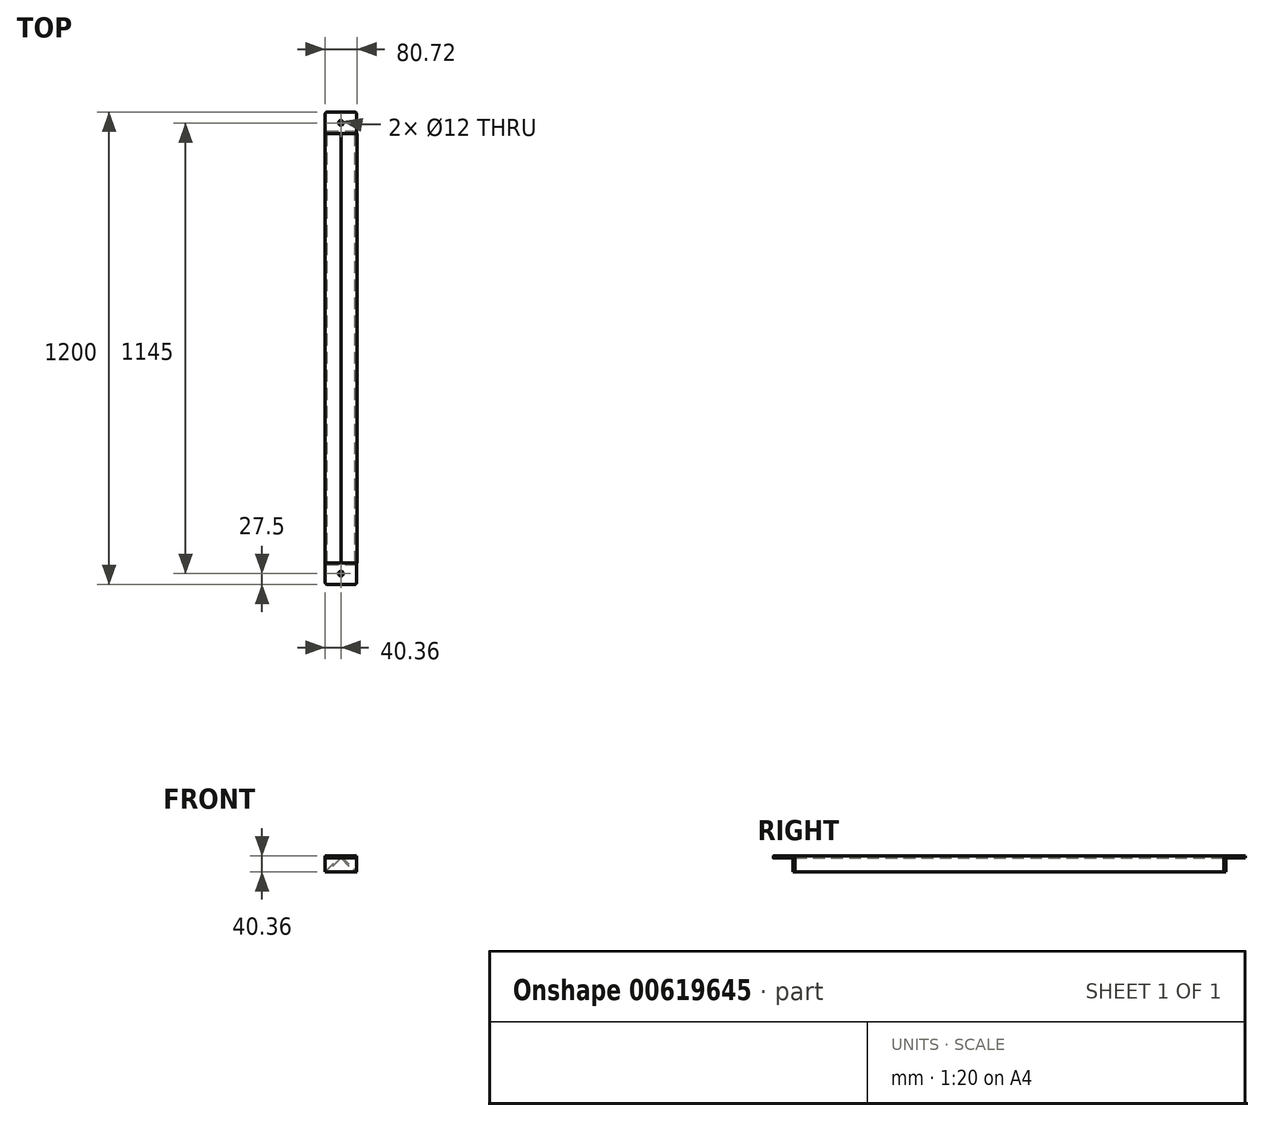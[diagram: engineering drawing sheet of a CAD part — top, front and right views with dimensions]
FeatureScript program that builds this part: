
annotation { "Feature Type Name" : "Feature", "Feature Type Description" : "" }
export const myFeature = defineFeature(function(context is Context, id is Id, definition is map)
    precondition{}
    {
        {
            var Q0;
            Q0=qCreatedBy(makeId("Front.planeOp"),FACE);
            var sketch = newSketch(context, id + "F0", { "sketchPlane" : qUnion([Q0])});
            skLineSegment(sketch, "E0", {"start": v(0, 0) * mm, "end": v(-35.36, -35.36) * mm});
            skLineSegment(sketch, "E1", {"start": v(0, 0) * mm, "end": v(35.36, -35.36) * mm});
            skLineSegment(sketch, "E2", {"start": v(-35.36, -35.36) * mm, "end": v(-40.36, -35.36) * mm});
            skLineSegment(sketch, "E3", {"start": v(-40.36, -35.36) * mm, "end": v(0, 5) * mm});
            skLineSegment(sketch, "E4", {"start": v(35.36, -35.36) * mm, "end": v(40.36, -35.36) * mm});
            skLineSegment(sketch, "E5", {"start": v(0, 5) * mm, "end": v(40.36, -35.36) * mm});
            skSolve(sketch);
        }
        {
            var Q0;
            Q0 = qSketchRegion(id + "F0", true);
            extrude(context, id + "F1", {"entities" : qUnion([Q0]), "depth" : 1090 * mm, "offsetDistance" : 25 * mm});
        }
        {
            var Q0;
            Q0=qCreatedBy(makeId("Right.planeOp"),FACE);
            var sketch = newSketch(context, id + "F2", { "sketchPlane" : qUnion([Q0])});
            skLineSegment(sketch, "E6.0", {"start": v(0, 5) * mm, "end": v(0, -35.36) * mm});
            skLineSegment(sketch, "E7", {"start": v(0, 5) * mm, "end": v(55, 5) * mm});
            skLineSegment(sketch, "E8", {"start": v(55, 5) * mm, "end": v(55, 0) * mm});
            skLineSegment(sketch, "E9", {"start": v(55, 0) * mm, "end": v(5, 0) * mm});
            skLineSegment(sketch, "E10", {"start": v(5, 0) * mm, "end": v(5, -35.36) * mm});
            skLineSegment(sketch, "E11", {"start": v(0, -35.36) * mm, "end": v(5, -35.36) * mm});
            skSolve(sketch);
        }
        {
            var Q0;
            Q0 = qSketchRegion(id + "F2", true);
            extrude(context, id + "F3", {"entities" : qUnion([Q0]), "endBound" : BoundingType.SYMMETRIC, "depth" : 80 * mm, "offsetDistance" : 25 * mm});
        }
        {
            var Q0;
            Q0=makeQuery(id+"F3.opExtrude","SWEPT_FACE",FACE,{"disambiguationData":[OSD([sQuery(id+"F2.wireOp",EDGE,"E7")])]});
            var sketch = newSketch(context, id + "F4", { "sketchPlane" : qUnion([Q0])});
            skPoint(sketch, "E12", {"position": v(0, 27.5) * mm});
            skPoint(sketch, "E12.positionSnap0", {"position": v(0, 55) * mm});
            skPoint(sketch, "E12.positionSnap1", {"position": v(-40, 27.5) * mm});
            skCircle(sketch, "E13", {"center": v(0, 27.5) * mm, "radius": 6 * mm});
            skSolve(sketch);
        }
        {
            var Q0;
            Q0 = qSketchRegion(id + "F4", true);
            extrude(context, id + "F5", {"entities" : qUnion([Q0]), "operationType" : NewBodyOperationType.REMOVE, "oppositeDirection" : true, "depth" : 25 * mm, "offsetDistance" : 25 * mm});
        }
        {
            var Q0;
            Q0=qCreatedBy(makeId("Front.planeOp"),FACE);
            cPlane(context, id + "F6", {"entities" : qUnion([Q0]), "cplaneType" : CPlaneType.OFFSET, "offset" : 545 * mm, "width" : 150 * mm, "height" : 150 * mm});
        }
        {
            var Q0;
            Q0=makeQuery(id+"F3.opExtrude","SWEPT_BODY",BODY,{"disambiguationData":[OSD([sQuery(id+"F2.wireOp",EDGE,"E6.0"),sQuery(id+"F2.wireOp",EDGE,"E7"),sQuery(id+"F2.wireOp",EDGE,"E8"),sQuery(id+"F2.wireOp",EDGE,"E9"),sQuery(id+"F2.wireOp",EDGE,"E10"),sQuery(id+"F2.wireOp",EDGE,"E11")])]});
            var Q1;
            Q1=qCreatedBy(id+"F6.planeOp",FACE);
            mirror(context, id + "F7", {"entities" : qUnion([Q0]), "mirrorPlane" : qUnion([Q1])});
        }
        {
            var Q0;
            Q0=makeQuery(id+"F3.opExtrude","CAP_EDGE",EDGE,{"disambiguationData":[OSD([sQuery(id+"F2.wireOp",EDGE,"E8")])],"isStart":true});
            var Q1;
            Q1=makeQuery(id+"F3.opExtrude","CAP_EDGE",EDGE,{"disambiguationData":[OSD([sQuery(id+"F2.wireOp",EDGE,"E8")])],"isStart":false});
            var Q2;
            Q2=makeQuery(id+"F7.opPattern","COPY",EDGE,{"derivedFrom":makeQuery(id+"F3.opExtrude","CAP_EDGE",EDGE,{"disambiguationData":[OSD([sQuery(id+"F2.wireOp",EDGE,"E8")])],"isStart":false}),"instanceName":"1"});
            var Q3;
            Q3=makeQuery(id+"F7.opPattern","COPY",EDGE,{"derivedFrom":makeQuery(id+"F3.opExtrude","CAP_EDGE",EDGE,{"disambiguationData":[OSD([sQuery(id+"F2.wireOp",EDGE,"E8")])],"isStart":true}),"instanceName":"1"});
            fillet(context, id + "F8", {"entities" : qUnion([Q0, Q1, Q2, Q3]), "radius" : 5 * mm, "tangentPropagation" : true, "allowEdgeOverflow" : false});
        }
    });
